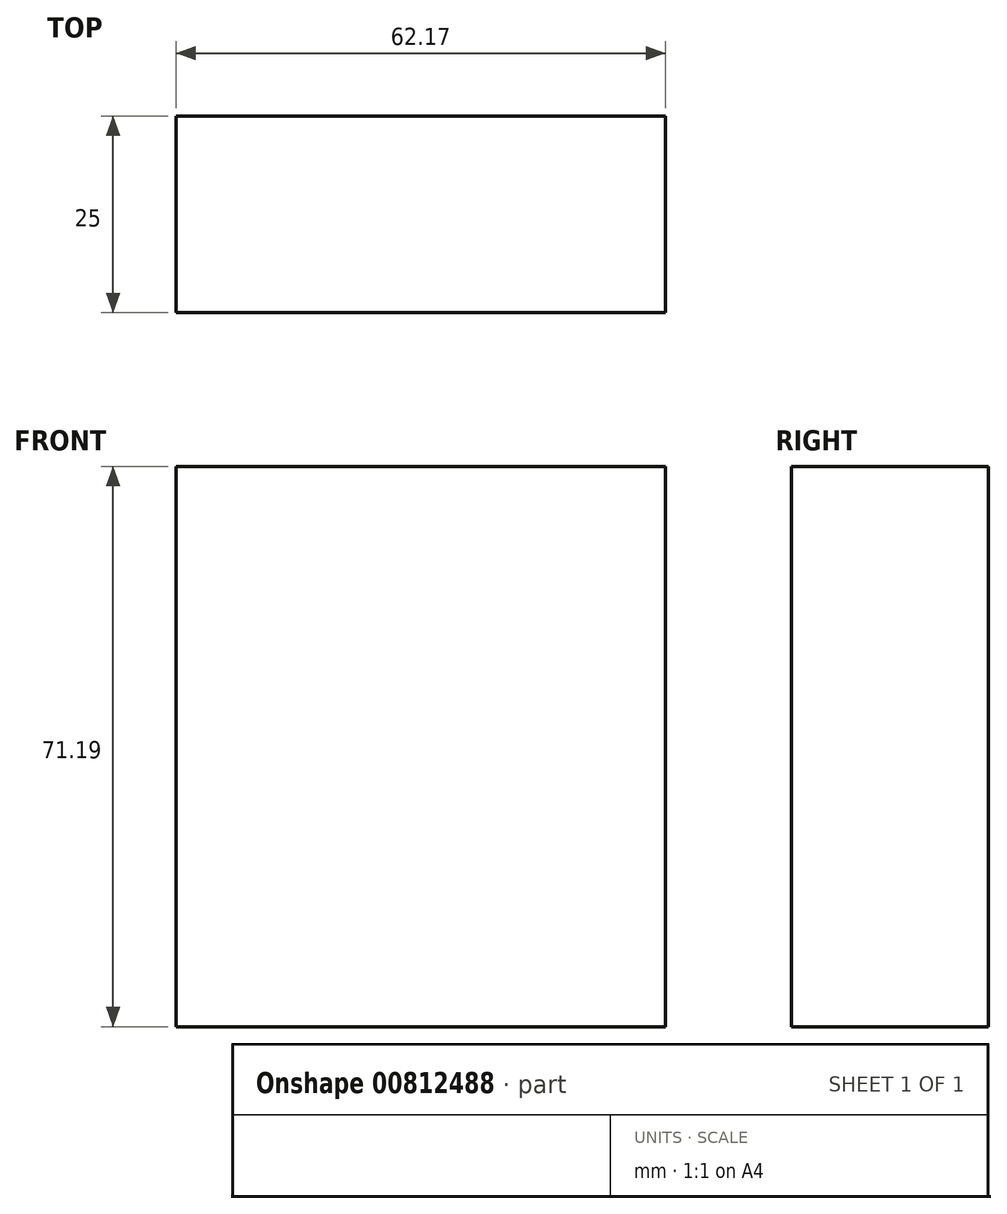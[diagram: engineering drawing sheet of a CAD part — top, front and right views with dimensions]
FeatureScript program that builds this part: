
annotation { "Feature Type Name" : "Feature", "Feature Type Description" : "" }
export const myFeature = defineFeature(function(context is Context, id is Id, definition is map)
    precondition{}
    {
        {
            var Q0;
            Q0=qCreatedBy(makeId("Front.planeOp"),FACE);
            var sketch = newSketch(context, id + "F0", { "sketchPlane" : qUnion([Q0])});
            skLineSegment(sketch, "E0.bottom", {"start": v(-23.31, 36.6) * mm, "end": v(38.86, 36.6) * mm});
            skLineSegment(sketch, "E0.top", {"start": v(-23.31, -34.6) * mm, "end": v(38.86, -34.6) * mm});
            skLineSegment(sketch, "E0.left", {"start": v(-23.31, 36.6) * mm, "end": v(-23.31, -34.6) * mm});
            skLineSegment(sketch, "E0.right", {"start": v(38.86, 36.6) * mm, "end": v(38.86, -34.6) * mm});
            skSolve(sketch);
        }
        {
            var Q0;
            Q0 = qSketchRegion(id + "F0", true);
            extrude(context, id + "F1", {"entities" : qUnion([Q0]), "depth" : 25 * mm, "offsetDistance" : 25 * mm});
        }
    });
